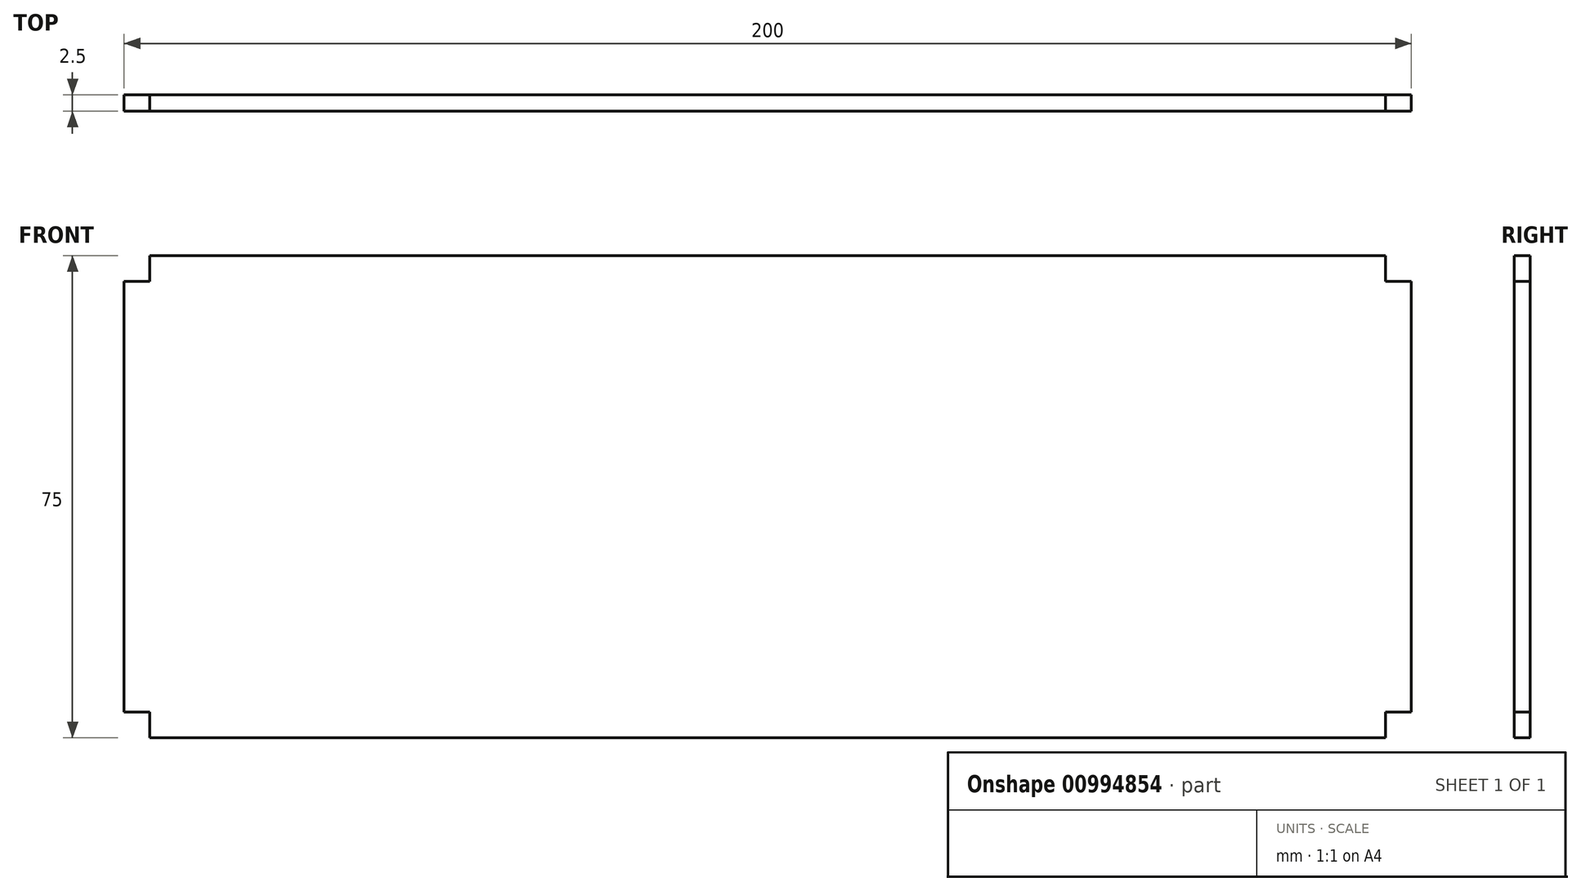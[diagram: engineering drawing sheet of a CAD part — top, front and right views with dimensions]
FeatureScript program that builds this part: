
annotation { "Feature Type Name" : "Feature", "Feature Type Description" : "" }
export const myFeature = defineFeature(function(context is Context, id is Id, definition is map)
    precondition{}
    {
        {
            var Q0;
            Q0=qCreatedBy(makeId("Front.planeOp"),FACE);
            var sketch = newSketch(context, id + "F0", { "sketchPlane" : qUnion([Q0])});
            skLineSegment(sketch, "E0", {"start": v(89.56, 7.76) * mm, "end": v(85.56, 7.76) * mm});
            skLineSegment(sketch, "E1", {"start": v(85.56, 7.76) * mm, "end": v(85.56, 11.76) * mm});
            skLineSegment(sketch, "E2", {"start": v(85.56, 11.76) * mm, "end": v(-10.44, 11.76) * mm});
            skLineSegment(sketch, "E3", {"start": v(89.56, 7.76) * mm, "end": v(89.56, -25.74) * mm});
            skLineSegment(sketch, "E4", {"start": v(-10.44, 41.88) * mm, "end": v(-10.44, -67.07) * mm, "construction": true});
            skLineSegment(sketch, "E5", {"start": v(81.95, -25.74) * mm, "end": v(-128.58, -25.74) * mm, "construction": true});
            skLineSegment(sketch, "E6.MirrorCS", {"start": v(-110.44, 7.76) * mm, "end": v(-106.44, 7.76) * mm});
            skLineSegment(sketch, "E7.MirrorCS", {"start": v(-106.44, 7.76) * mm, "end": v(-106.44, 11.76) * mm});
            skLineSegment(sketch, "E8.MirrorCS", {"start": v(-106.44, 11.76) * mm, "end": v(-10.44, 11.76) * mm});
            skLineSegment(sketch, "E9.MirrorCS", {"start": v(-110.44, 7.76) * mm, "end": v(-110.44, -25.74) * mm});
            skLineSegment(sketch, "E10.MirrorCS", {"start": v(89.56, -59.24) * mm, "end": v(85.56, -59.24) * mm});
            skLineSegment(sketch, "E11.MirrorCS", {"start": v(-106.44, -59.24) * mm, "end": v(-106.44, -63.24) * mm});
            skLineSegment(sketch, "E12.MirrorCS", {"start": v(85.56, -59.24) * mm, "end": v(85.56, -63.24) * mm});
            skLineSegment(sketch, "E13.MirrorCS", {"start": v(-110.44, -59.24) * mm, "end": v(-106.44, -59.24) * mm});
            skLineSegment(sketch, "E14.MirrorCS", {"start": v(85.56, -63.24) * mm, "end": v(-10.44, -63.24) * mm});
            skLineSegment(sketch, "E15.MirrorCS", {"start": v(89.56, -59.24) * mm, "end": v(89.56, -25.74) * mm});
            skLineSegment(sketch, "E16.MirrorCS", {"start": v(-110.44, -59.24) * mm, "end": v(-110.44, -25.74) * mm});
            skLineSegment(sketch, "E17.MirrorCS", {"start": v(-106.44, -63.24) * mm, "end": v(-10.44, -63.24) * mm});
            skSolve(sketch);
        }
        {
            var Q0;
            Q0 = qSketchRegion(id + "F0", true);
            extrude(context, id + "F1", {"entities" : qUnion([Q0]), "depth" : 2.5 * mm, "offsetDistance" : 25 * mm});
        }
    });
